# Revit family: EN 220TJ + STV
name_source: partatom
category: Equipement spécialisé
units: mm (PartAtom-declared; Revit-internal decimal feet)

## family parameters
Basée sur le plan de construction = Non
Cote de connecteur circulaire = Utiliser le diamètre
Couper avec des vides une fois chargée = Non
Numéro OmniClass = 23.50.00.00
Partagée = Non
Point de calcul de pièce = Non
Titre OmniClass = Conveying Systems & Material Handling
Toujours verticalement = Oui
Type d'élément = Normal

## types (1)
- 220 TJ+
    Average consumption (L/h) = 1.885
    CO2 emissions (g/kWh) = 5
    Counterweight offset (turret at 90°) = 1.34 m
    Créé par = ATLANCAD
    Description = Nacelle élévatrice télescopique tout-terrain
    Elévation par défaut = 0.00 m
    Engine norm = Stage V
    External turning radius = 4.40 m
    Fabricant = MANITOU
    Floor height (access) = 0.39 m
    Ground clearance = 0.38 m
    Ground clearance at centre of wheelbase = 0.44 m
    I.C. Engine power rating - Power (ch) = 36.2
    I.C. Engine power rating - Power (kW) = 27.5
    Internal turning radius (over tyres) = 2.00 m
    Jib length = 2.00 m
    Max. lifting height = 21.74 m
    Max. outreach = 17.79 m
    Modèle = 220 TJ+
    Noise to environment (LwA) = 105
    Number of people (inside) = 3
    Number of people (outside) = 3
    Overall height (stowed) = 3.03 m
    Overall height (transport) = 2.67 m
    Overall lenght (stowed) = 7.35 m
    Overall lenght (transport) = 9.81 m
    Permissible leveling = 4.00°
    Platform capacity = 400.00 kg
    Platform dimensions (length) = 2.30 m
    Platform dimensions (width) = 0.90 m
    Platform weight = 13600.00 kg
    URL = www.manitou.com
    Wheelbase = 2.80 m
    Width = 2.48 m
